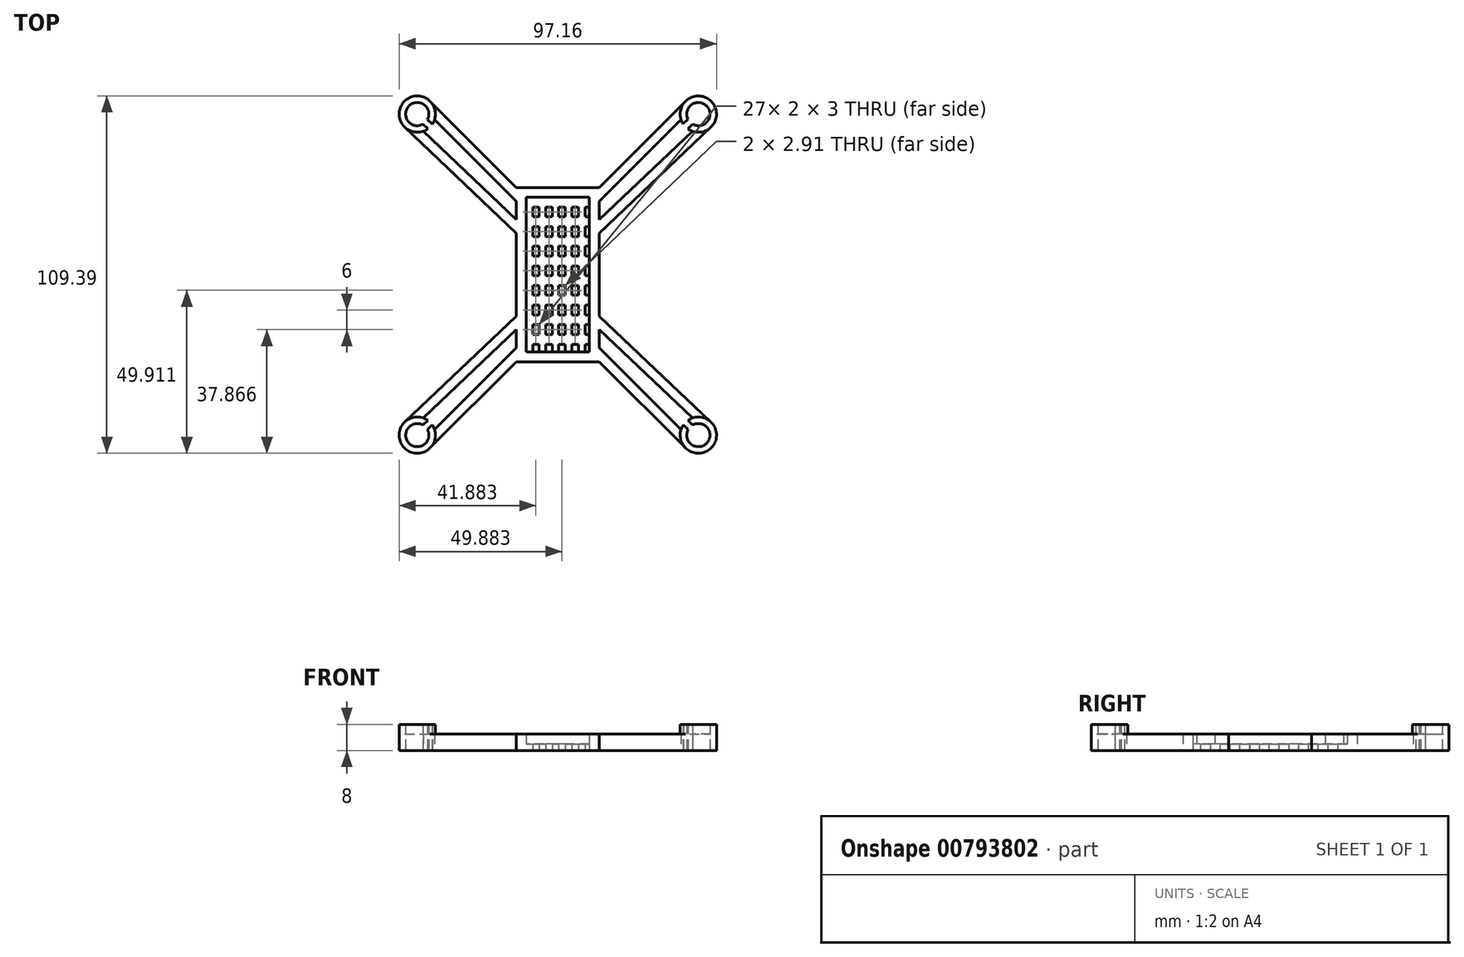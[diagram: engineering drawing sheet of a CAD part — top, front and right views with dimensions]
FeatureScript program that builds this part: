
annotation { "Feature Type Name" : "Feature", "Feature Type Description" : "" }
export const myFeature = defineFeature(function(context is Context, id is Id, definition is map)
    precondition{}
    {
        {
            var Q0;
            Q0=qCreatedBy(makeId("Top.planeOp"),FACE);
            var sketch = newSketch(context, id + "F0", { "sketchPlane" : qUnion([Q0])});
            skArc(sketch, "E0", {"start": v(4.6, 95.16) * mm, "mid": v(5, 95.85) * mm, "end": v(5.3, 96.6) * mm});
            skLineSegment(sketch, "E1", {"start": v(30.32, 71.56) * mm, "end": v(30.32, 65.97) * mm});
            skLineSegment(sketch, "E2", {"start": v(30.32, 22.47) * mm, "end": v(55.72, 22.47) * mm});
            skLineSegment(sketch, "E3", {"start": v(55.72, 26.7) * mm, "end": v(55.72, 32.3) * mm});
            skLineSegment(sketch, "E4", {"start": v(55.72, 75.8) * mm, "end": v(30.32, 75.8) * mm});
            skLineSegment(sketch, "E5", {"start": v(3.93, 102.2) * mm, "end": v(30.32, 75.8) * mm});
            skLineSegment(sketch, "E6", {"start": v(-3.82, 94.24) * mm, "end": v(30.32, 61.84) * mm});
            skLineSegment(sketch, "E7", {"start": v(55.72, 75.8) * mm, "end": v(82.12, 102.2) * mm});
            skLineSegment(sketch, "E8", {"start": v(55.72, 61.84) * mm, "end": v(89.87, 94.24) * mm});
            skArc(sketch, "E9", {"start": v(89.87, 94.24) * mm, "mid": v(90.03, 102.15) * mm, "end": v(82.12, 102.2) * mm});
            skLineSegment(sketch, "E10", {"start": v(30.32, 22.47) * mm, "end": v(3.93, -3.93) * mm});
            skLineSegment(sketch, "E11", {"start": v(30.32, 36.44) * mm, "end": v(-3.82, 4.03) * mm});
            skArc(sketch, "E12", {"start": v(5.3, 1.68) * mm, "mid": v(4.99, 2.45) * mm, "end": v(4.57, 3.17) * mm});
            skLineSegment(sketch, "E13", {"start": v(55.72, 22.47) * mm, "end": v(82.12, -3.93) * mm});
            skLineSegment(sketch, "E14", {"start": v(55.72, 36.44) * mm, "end": v(89.87, 4.03) * mm});
            skArc(sketch, "E15", {"start": v(84.23, 5.25) * mm, "mid": v(83.5, 4.94) * mm, "end": v(82.82, 4.52) * mm});
            skArc(sketch, "E16.0", {"start": v(3.15, 96.62) * mm, "mid": v(-2.55, 100.75) * mm, "end": v(1.74, 95.17) * mm});
            skArc(sketch, "E17.0", {"start": v(1.74, 3.1) * mm, "mid": v(-2.53, -2.5) * mm, "end": v(3.13, 1.7) * mm});
            skArc(sketch, "E18.0", {"start": v(84.31, 95.17) * mm, "mid": v(88.63, 100.72) * mm, "end": v(82.86, 96.7) * mm});
            skArc(sketch, "E19.0", {"start": v(82.9, 1.66) * mm, "mid": v(88.6, -2.48) * mm, "end": v(84.3, 3.1) * mm});
            skLineSegment(sketch, "E20.0", {"start": v(5.3, 96.6) * mm, "end": v(30.32, 71.56) * mm});
            skLineSegment(sketch, "E21.0", {"start": v(1.82, 93.02) * mm, "end": v(30.32, 65.97) * mm});
            skLineSegment(sketch, "E22.0", {"start": v(55.72, 71.56) * mm, "end": v(80.75, 96.6) * mm});
            skLineSegment(sketch, "E23.0", {"start": v(55.72, 65.97) * mm, "end": v(84.23, 93.02) * mm});
            skLineSegment(sketch, "E24.0", {"start": v(55.72, 32.3) * mm, "end": v(84.23, 5.25) * mm});
            skLineSegment(sketch, "E25.0", {"start": v(30.32, 32.3) * mm, "end": v(1.82, 5.25) * mm});
            skLineSegment(sketch, "E26.0", {"start": v(30.32, 26.7) * mm, "end": v(5.3, 1.68) * mm});
            skLineSegment(sketch, "E27.0", {"start": v(55.72, 26.7) * mm, "end": v(80.75, 1.68) * mm});
            skLineSegment(sketch, "E28", {"start": v(81.36, 95.28) * mm, "end": v(82.86, 96.7) * mm});
            skLineSegment(sketch, "E29", {"start": v(82.82, 93.75) * mm, "end": v(84.31, 95.17) * mm});
            skLineSegment(sketch, "E30", {"start": v(3.23, 93.75) * mm, "end": v(1.74, 95.17) * mm});
            skLineSegment(sketch, "E31", {"start": v(4.6, 95.16) * mm, "end": v(3.15, 96.62) * mm});
            skLineSegment(sketch, "E32", {"start": v(3.23, 4.52) * mm, "end": v(1.74, 3.1) * mm});
            skLineSegment(sketch, "E33", {"start": v(4.57, 3.17) * mm, "end": v(3.13, 1.7) * mm});
            skLineSegment(sketch, "E34", {"start": v(82.82, 4.52) * mm, "end": v(84.3, 3.1) * mm});
            skLineSegment(sketch, "E35", {"start": v(81.44, 3.11) * mm, "end": v(82.9, 1.66) * mm});
            skArc(sketch, "E36.trimOffspring", {"start": v(82.12, -3.93) * mm, "mid": v(90.03, -3.88) * mm, "end": v(89.87, 4.03) * mm});
            skArc(sketch, "E37.trimOffspring", {"start": v(81.44, 3.11) * mm, "mid": v(81.05, 2.42) * mm, "end": v(80.75, 1.68) * mm});
            skLineSegment(sketch, "E38.trimOffspring", {"start": v(55.72, 36.44) * mm, "end": v(55.72, 61.84) * mm});
            skLineSegment(sketch, "E39.trimOffspring", {"start": v(30.32, 61.84) * mm, "end": v(30.32, 36.44) * mm});
            skLineSegment(sketch, "E40.trimOffspring", {"start": v(55.72, 65.97) * mm, "end": v(55.72, 71.56) * mm});
            skLineSegment(sketch, "E41.trimOffspring", {"start": v(30.32, 32.3) * mm, "end": v(30.32, 26.7) * mm});
            skArc(sketch, "E42.trimOffspring", {"start": v(-3.82, 4.03) * mm, "mid": v(-3.98, -3.88) * mm, "end": v(3.93, -3.93) * mm});
            skArc(sketch, "E43.trimOffspring", {"start": v(3.23, 4.52) * mm, "mid": v(2.55, 4.94) * mm, "end": v(1.82, 5.25) * mm});
            skArc(sketch, "E44.trimOffspring", {"start": v(1.82, 93.02) * mm, "mid": v(2.55, 93.33) * mm, "end": v(3.23, 93.75) * mm});
            skArc(sketch, "E45.trimOffspring", {"start": v(3.93, 102.2) * mm, "mid": v(-3.98, 102.15) * mm, "end": v(-3.82, 94.24) * mm});
            skArc(sketch, "E46.trimOffspring", {"start": v(80.75, 96.6) * mm, "mid": v(81.01, 95.92) * mm, "end": v(81.36, 95.28) * mm});
            skArc(sketch, "E47.trimOffspring", {"start": v(82.82, 93.75) * mm, "mid": v(83.5, 93.33) * mm, "end": v(84.23, 93.02) * mm});
            skLineSegment(sketch, "E48", {"start": v(33.32, 72.8) * mm, "end": v(33.32, 25.47) * mm});
            skLineSegment(sketch, "E49", {"start": v(33.32, 25.47) * mm, "end": v(52.72, 25.47) * mm});
            skLineSegment(sketch, "E50", {"start": v(52.72, 25.47) * mm, "end": v(52.72, 72.8) * mm});
            skLineSegment(sketch, "E51", {"start": v(52.72, 72.8) * mm, "end": v(33.32, 72.8) * mm});
            skArc(sketch, "E52", {"start": v(84.23, 93.02) * mm, "mid": v(87.22, 92.84) * mm, "end": v(89.87, 94.24) * mm});
            skArc(sketch, "E53", {"start": v(82.12, 102.2) * mm, "mid": v(80.65, 99.59) * mm, "end": v(80.75, 96.6) * mm});
            skArc(sketch, "E54", {"start": v(5.3, 96.6) * mm, "mid": v(5.4, 99.59) * mm, "end": v(3.93, 102.2) * mm});
            skArc(sketch, "E55", {"start": v(-3.82, 94.24) * mm, "mid": v(-1.17, 92.84) * mm, "end": v(1.82, 93.02) * mm});
            skArc(sketch, "E56", {"start": v(3.93, -3.93) * mm, "mid": v(5.4, -1.32) * mm, "end": v(5.3, 1.68) * mm});
            skArc(sketch, "E57", {"start": v(1.82, 5.25) * mm, "mid": v(-1.17, 5.43) * mm, "end": v(-3.82, 4.03) * mm});
            skArc(sketch, "E58", {"start": v(80.75, 1.68) * mm, "mid": v(80.65, -1.32) * mm, "end": v(82.12, -3.93) * mm});
            skArc(sketch, "E59", {"start": v(89.87, 4.03) * mm, "mid": v(87.22, 5.43) * mm, "end": v(84.23, 5.25) * mm});
            skLineSegment(sketch, "E60.bottom", {"start": v(35.32, 69.8) * mm, "end": v(37.32, 69.8) * mm});
            skLineSegment(sketch, "E60.top", {"start": v(35.32, 66.8) * mm, "end": v(37.32, 66.8) * mm});
            skLineSegment(sketch, "E60.left", {"start": v(35.32, 69.8) * mm, "end": v(35.32, 66.8) * mm});
            skLineSegment(sketch, "E60.right", {"start": v(37.32, 69.8) * mm, "end": v(37.32, 66.8) * mm});
            skLineSegment(sketch, "E61.bottom", {"start": v(35.32, 63.8) * mm, "end": v(37.32, 63.8) * mm});
            skLineSegment(sketch, "E61.top", {"start": v(35.32, 60.8) * mm, "end": v(37.32, 60.8) * mm});
            skLineSegment(sketch, "E61.left", {"start": v(35.32, 63.8) * mm, "end": v(35.32, 60.8) * mm});
            skLineSegment(sketch, "E61.right", {"start": v(37.32, 63.8) * mm, "end": v(37.32, 60.8) * mm});
            skLineSegment(sketch, "E62.bottom", {"start": v(35.32, 57.8) * mm, "end": v(37.32, 57.8) * mm});
            skLineSegment(sketch, "E62.top", {"start": v(35.32, 54.8) * mm, "end": v(37.32, 54.8) * mm});
            skLineSegment(sketch, "E62.left", {"start": v(35.32, 57.8) * mm, "end": v(35.32, 54.8) * mm});
            skLineSegment(sketch, "E62.right", {"start": v(37.32, 57.8) * mm, "end": v(37.32, 54.8) * mm});
            skLineSegment(sketch, "E63.bottom", {"start": v(35.32, 51.8) * mm, "end": v(37.32, 51.8) * mm});
            skLineSegment(sketch, "E63.top", {"start": v(35.32, 48.8) * mm, "end": v(37.32, 48.8) * mm});
            skLineSegment(sketch, "E63.left", {"start": v(35.32, 51.8) * mm, "end": v(35.32, 48.8) * mm});
            skLineSegment(sketch, "E63.right", {"start": v(37.32, 51.8) * mm, "end": v(37.32, 48.8) * mm});
            skLineSegment(sketch, "E64.bottom", {"start": v(35.32, 45.8) * mm, "end": v(37.32, 45.8) * mm});
            skLineSegment(sketch, "E64.top", {"start": v(35.32, 42.8) * mm, "end": v(37.32, 42.8) * mm});
            skLineSegment(sketch, "E64.left", {"start": v(35.32, 45.8) * mm, "end": v(35.32, 42.8) * mm});
            skLineSegment(sketch, "E64.right", {"start": v(37.32, 45.8) * mm, "end": v(37.32, 42.8) * mm});
            skLineSegment(sketch, "E65.bottom", {"start": v(35.32, 39.8) * mm, "end": v(37.32, 39.8) * mm});
            skLineSegment(sketch, "E65.top", {"start": v(35.32, 36.8) * mm, "end": v(37.32, 36.8) * mm});
            skLineSegment(sketch, "E65.left", {"start": v(35.32, 39.8) * mm, "end": v(35.32, 36.8) * mm});
            skLineSegment(sketch, "E65.right", {"start": v(37.32, 39.8) * mm, "end": v(37.32, 36.8) * mm});
            skLineSegment(sketch, "E66.bottom", {"start": v(35.32, 33.8) * mm, "end": v(37.32, 33.8) * mm});
            skLineSegment(sketch, "E66.top", {"start": v(35.32, 30.8) * mm, "end": v(37.32, 30.8) * mm});
            skLineSegment(sketch, "E66.left", {"start": v(35.32, 33.8) * mm, "end": v(35.32, 30.8) * mm});
            skLineSegment(sketch, "E66.right", {"start": v(37.32, 33.8) * mm, "end": v(37.32, 30.8) * mm});
            skLineSegment(sketch, "E67.bottom", {"start": v(35.32, 27.8) * mm, "end": v(37.32, 27.8) * mm});
            skLineSegment(sketch, "E67.top", {"start": v(35.32, 25.47) * mm, "end": v(37.32, 25.47) * mm});
            skLineSegment(sketch, "E67.left", {"start": v(35.32, 27.8) * mm, "end": v(35.32, 25.47) * mm});
            skLineSegment(sketch, "E67.right", {"start": v(37.32, 27.8) * mm, "end": v(37.32, 25.47) * mm});
            skLineSegment(sketch, "E68.bottom", {"start": v(39.32, 27.8) * mm, "end": v(41.32, 27.8) * mm});
            skLineSegment(sketch, "E68.top", {"start": v(39.32, 25.47) * mm, "end": v(41.32, 25.47) * mm});
            skLineSegment(sketch, "E68.left", {"start": v(39.32, 27.8) * mm, "end": v(39.32, 25.47) * mm});
            skLineSegment(sketch, "E68.right", {"start": v(41.32, 27.8) * mm, "end": v(41.32, 25.47) * mm});
            skLineSegment(sketch, "E69.bottom", {"start": v(43.32, 27.8) * mm, "end": v(45.32, 27.8) * mm});
            skLineSegment(sketch, "E69.top", {"start": v(43.32, 25.47) * mm, "end": v(45.32, 25.47) * mm});
            skLineSegment(sketch, "E69.left", {"start": v(43.32, 27.8) * mm, "end": v(43.32, 25.47) * mm});
            skLineSegment(sketch, "E69.right", {"start": v(45.32, 27.8) * mm, "end": v(45.32, 25.47) * mm});
            skLineSegment(sketch, "E70.bottom", {"start": v(47.32, 27.8) * mm, "end": v(49.32, 27.8) * mm});
            skLineSegment(sketch, "E70.top", {"start": v(47.32, 25.47) * mm, "end": v(49.32, 25.47) * mm});
            skLineSegment(sketch, "E70.left", {"start": v(47.32, 27.8) * mm, "end": v(47.32, 25.47) * mm});
            skLineSegment(sketch, "E70.right", {"start": v(49.32, 27.8) * mm, "end": v(49.32, 25.47) * mm});
            skLineSegment(sketch, "E71.bottom", {"start": v(51.32, 27.8) * mm, "end": v(52.72, 27.8) * mm});
            skLineSegment(sketch, "E71.top", {"start": v(51.32, 25.47) * mm, "end": v(52.72, 25.47) * mm});
            skLineSegment(sketch, "E71.left", {"start": v(51.32, 27.8) * mm, "end": v(51.32, 25.47) * mm});
            skLineSegment(sketch, "E71.right", {"start": v(52.72, 27.8) * mm, "end": v(52.72, 25.47) * mm});
            skLineSegment(sketch, "E72.bottom", {"start": v(51.32, 33.8) * mm, "end": v(52.72, 33.8) * mm});
            skLineSegment(sketch, "E72.top", {"start": v(51.32, 30.8) * mm, "end": v(52.72, 30.8) * mm});
            skLineSegment(sketch, "E72.left", {"start": v(51.32, 33.8) * mm, "end": v(51.32, 30.8) * mm});
            skLineSegment(sketch, "E72.right", {"start": v(52.72, 33.8) * mm, "end": v(52.72, 30.8) * mm});
            skLineSegment(sketch, "E73.bottom", {"start": v(47.32, 33.8) * mm, "end": v(49.32, 33.8) * mm});
            skLineSegment(sketch, "E73.top", {"start": v(47.32, 30.8) * mm, "end": v(49.32, 30.8) * mm});
            skLineSegment(sketch, "E73.left", {"start": v(47.32, 33.8) * mm, "end": v(47.32, 30.8) * mm});
            skLineSegment(sketch, "E73.right", {"start": v(49.32, 33.8) * mm, "end": v(49.32, 30.8) * mm});
            skLineSegment(sketch, "E74.bottom", {"start": v(45.32, 33.8) * mm, "end": v(43.32, 33.8) * mm});
            skLineSegment(sketch, "E74.top", {"start": v(45.32, 30.8) * mm, "end": v(43.32, 30.8) * mm});
            skLineSegment(sketch, "E74.left", {"start": v(45.32, 33.8) * mm, "end": v(45.32, 30.8) * mm});
            skLineSegment(sketch, "E74.right", {"start": v(43.32, 33.8) * mm, "end": v(43.32, 30.8) * mm});
            skLineSegment(sketch, "E75.bottom", {"start": v(41.32, 33.8) * mm, "end": v(39.32, 33.8) * mm});
            skLineSegment(sketch, "E75.top", {"start": v(41.32, 30.8) * mm, "end": v(39.32, 30.8) * mm});
            skLineSegment(sketch, "E75.left", {"start": v(41.32, 33.8) * mm, "end": v(41.32, 30.8) * mm});
            skLineSegment(sketch, "E75.right", {"start": v(39.32, 33.8) * mm, "end": v(39.32, 30.8) * mm});
            skLineSegment(sketch, "E76.bottom", {"start": v(39.32, 36.8) * mm, "end": v(41.32, 36.8) * mm});
            skLineSegment(sketch, "E76.top", {"start": v(39.32, 39.8) * mm, "end": v(41.32, 39.8) * mm});
            skLineSegment(sketch, "E76.left", {"start": v(39.32, 36.8) * mm, "end": v(39.32, 39.8) * mm});
            skLineSegment(sketch, "E76.right", {"start": v(41.32, 36.8) * mm, "end": v(41.32, 39.8) * mm});
            skLineSegment(sketch, "E77.bottom", {"start": v(43.32, 39.8) * mm, "end": v(45.32, 39.8) * mm});
            skLineSegment(sketch, "E77.top", {"start": v(43.32, 36.8) * mm, "end": v(45.32, 36.8) * mm});
            skLineSegment(sketch, "E77.left", {"start": v(43.32, 39.8) * mm, "end": v(43.32, 36.8) * mm});
            skLineSegment(sketch, "E77.right", {"start": v(45.32, 39.8) * mm, "end": v(45.32, 36.8) * mm});
            skLineSegment(sketch, "E78.bottom", {"start": v(47.32, 36.8) * mm, "end": v(49.32, 36.8) * mm});
            skLineSegment(sketch, "E78.top", {"start": v(47.32, 39.8) * mm, "end": v(49.32, 39.8) * mm});
            skLineSegment(sketch, "E78.left", {"start": v(47.32, 36.8) * mm, "end": v(47.32, 39.8) * mm});
            skLineSegment(sketch, "E78.right", {"start": v(49.32, 36.8) * mm, "end": v(49.32, 39.8) * mm});
            skLineSegment(sketch, "E79.bottom", {"start": v(51.32, 39.8) * mm, "end": v(52.72, 39.8) * mm});
            skLineSegment(sketch, "E79.top", {"start": v(51.32, 36.8) * mm, "end": v(52.72, 36.8) * mm});
            skLineSegment(sketch, "E79.left", {"start": v(51.32, 39.8) * mm, "end": v(51.32, 36.8) * mm});
            skLineSegment(sketch, "E79.right", {"start": v(52.72, 39.8) * mm, "end": v(52.72, 36.8) * mm});
            skLineSegment(sketch, "E80.bottom", {"start": v(52.72, 42.8) * mm, "end": v(51.32, 42.8) * mm});
            skLineSegment(sketch, "E80.top", {"start": v(52.72, 45.8) * mm, "end": v(51.32, 45.8) * mm});
            skLineSegment(sketch, "E80.left", {"start": v(52.72, 42.8) * mm, "end": v(52.72, 45.8) * mm});
            skLineSegment(sketch, "E80.right", {"start": v(51.32, 42.8) * mm, "end": v(51.32, 45.8) * mm});
            skLineSegment(sketch, "E81.bottom", {"start": v(49.32, 45.8) * mm, "end": v(47.32, 45.8) * mm});
            skLineSegment(sketch, "E81.top", {"start": v(49.32, 42.8) * mm, "end": v(47.32, 42.8) * mm});
            skLineSegment(sketch, "E81.left", {"start": v(49.32, 45.8) * mm, "end": v(49.32, 42.8) * mm});
            skLineSegment(sketch, "E81.right", {"start": v(47.32, 45.8) * mm, "end": v(47.32, 42.8) * mm});
            skLineSegment(sketch, "E82.bottom", {"start": v(45.32, 42.9) * mm, "end": v(43.32, 42.9) * mm});
            skLineSegment(sketch, "E82.top", {"start": v(45.32, 45.8) * mm, "end": v(43.32, 45.8) * mm});
            skLineSegment(sketch, "E82.left", {"start": v(45.32, 42.9) * mm, "end": v(45.32, 45.8) * mm});
            skLineSegment(sketch, "E82.right", {"start": v(43.32, 42.9) * mm, "end": v(43.32, 45.8) * mm});
            skLineSegment(sketch, "E83.bottom", {"start": v(41.32, 45.8) * mm, "end": v(39.32, 45.8) * mm});
            skLineSegment(sketch, "E83.top", {"start": v(41.32, 42.8) * mm, "end": v(39.32, 42.8) * mm});
            skLineSegment(sketch, "E83.left", {"start": v(41.32, 45.8) * mm, "end": v(41.32, 42.8) * mm});
            skLineSegment(sketch, "E83.right", {"start": v(39.32, 45.8) * mm, "end": v(39.32, 42.8) * mm});
            skLineSegment(sketch, "E84.bottom", {"start": v(39.32, 51.8) * mm, "end": v(41.32, 51.8) * mm});
            skLineSegment(sketch, "E84.top", {"start": v(39.32, 48.8) * mm, "end": v(41.32, 48.8) * mm});
            skLineSegment(sketch, "E84.left", {"start": v(39.32, 51.8) * mm, "end": v(39.32, 48.8) * mm});
            skLineSegment(sketch, "E84.right", {"start": v(41.32, 51.8) * mm, "end": v(41.32, 48.8) * mm});
            skLineSegment(sketch, "E85.bottom", {"start": v(43.32, 48.8) * mm, "end": v(45.32, 48.8) * mm});
            skLineSegment(sketch, "E85.top", {"start": v(43.32, 51.8) * mm, "end": v(45.32, 51.8) * mm});
            skLineSegment(sketch, "E85.left", {"start": v(43.32, 48.8) * mm, "end": v(43.32, 51.8) * mm});
            skLineSegment(sketch, "E85.right", {"start": v(45.32, 48.8) * mm, "end": v(45.32, 51.8) * mm});
            skLineSegment(sketch, "E86.bottom", {"start": v(47.32, 51.8) * mm, "end": v(49.32, 51.8) * mm});
            skLineSegment(sketch, "E86.top", {"start": v(47.32, 48.8) * mm, "end": v(49.32, 48.8) * mm});
            skLineSegment(sketch, "E86.left", {"start": v(47.32, 51.8) * mm, "end": v(47.32, 48.8) * mm});
            skLineSegment(sketch, "E86.right", {"start": v(49.32, 51.8) * mm, "end": v(49.32, 48.8) * mm});
            skLineSegment(sketch, "E87.bottom", {"start": v(51.4, 51.8) * mm, "end": v(52.72, 51.8) * mm});
            skLineSegment(sketch, "E87.top", {"start": v(51.4, 48.8) * mm, "end": v(52.72, 48.8) * mm});
            skLineSegment(sketch, "E87.left", {"start": v(51.4, 51.8) * mm, "end": v(51.4, 48.8) * mm});
            skLineSegment(sketch, "E87.right", {"start": v(52.72, 51.8) * mm, "end": v(52.72, 48.8) * mm});
            skLineSegment(sketch, "E88.bottom", {"start": v(52.72, 54.8) * mm, "end": v(51.32, 54.8) * mm});
            skLineSegment(sketch, "E88.top", {"start": v(52.72, 57.8) * mm, "end": v(51.32, 57.8) * mm});
            skLineSegment(sketch, "E88.left", {"start": v(52.72, 54.8) * mm, "end": v(52.72, 57.8) * mm});
            skLineSegment(sketch, "E88.right", {"start": v(51.32, 54.8) * mm, "end": v(51.32, 57.8) * mm});
            skLineSegment(sketch, "E89.bottom", {"start": v(49.32, 57.8) * mm, "end": v(47.32, 57.8) * mm});
            skLineSegment(sketch, "E89.top", {"start": v(49.32, 54.8) * mm, "end": v(47.32, 54.8) * mm});
            skLineSegment(sketch, "E89.left", {"start": v(49.32, 57.8) * mm, "end": v(49.32, 54.8) * mm});
            skLineSegment(sketch, "E89.right", {"start": v(47.32, 57.8) * mm, "end": v(47.32, 54.8) * mm});
            skLineSegment(sketch, "E90.bottom", {"start": v(45.32, 54.8) * mm, "end": v(43.32, 54.8) * mm});
            skLineSegment(sketch, "E90.top", {"start": v(45.32, 57.8) * mm, "end": v(43.32, 57.8) * mm});
            skLineSegment(sketch, "E90.left", {"start": v(45.32, 54.8) * mm, "end": v(45.32, 57.8) * mm});
            skLineSegment(sketch, "E90.right", {"start": v(43.32, 54.8) * mm, "end": v(43.32, 57.8) * mm});
            skLineSegment(sketch, "E91.bottom", {"start": v(41.32, 57.8) * mm, "end": v(39.32, 57.8) * mm});
            skLineSegment(sketch, "E91.top", {"start": v(41.32, 54.8) * mm, "end": v(39.32, 54.8) * mm});
            skLineSegment(sketch, "E91.left", {"start": v(41.32, 57.8) * mm, "end": v(41.32, 54.8) * mm});
            skLineSegment(sketch, "E91.right", {"start": v(39.32, 57.8) * mm, "end": v(39.32, 54.8) * mm});
            skLineSegment(sketch, "E92.bottom", {"start": v(39.32, 60.8) * mm, "end": v(41.32, 60.8) * mm});
            skLineSegment(sketch, "E92.top", {"start": v(39.32, 63.8) * mm, "end": v(41.32, 63.8) * mm});
            skLineSegment(sketch, "E92.left", {"start": v(39.32, 60.8) * mm, "end": v(39.32, 63.8) * mm});
            skLineSegment(sketch, "E92.right", {"start": v(41.32, 60.8) * mm, "end": v(41.32, 63.8) * mm});
            skLineSegment(sketch, "E93.bottom", {"start": v(43.32, 63.8) * mm, "end": v(45.32, 63.8) * mm});
            skLineSegment(sketch, "E93.top", {"start": v(43.32, 60.8) * mm, "end": v(45.32, 60.8) * mm});
            skLineSegment(sketch, "E93.left", {"start": v(43.32, 63.8) * mm, "end": v(43.32, 60.8) * mm});
            skLineSegment(sketch, "E93.right", {"start": v(45.32, 63.8) * mm, "end": v(45.32, 60.8) * mm});
            skLineSegment(sketch, "E94.bottom", {"start": v(47.32, 63.8) * mm, "end": v(49.32, 63.8) * mm});
            skLineSegment(sketch, "E94.top", {"start": v(47.32, 60.8) * mm, "end": v(49.32, 60.8) * mm});
            skLineSegment(sketch, "E94.left", {"start": v(47.32, 63.8) * mm, "end": v(47.32, 60.8) * mm});
            skLineSegment(sketch, "E94.right", {"start": v(49.32, 63.8) * mm, "end": v(49.32, 60.8) * mm});
            skLineSegment(sketch, "E95.bottom", {"start": v(51.32, 60.8) * mm, "end": v(52.72, 60.8) * mm});
            skLineSegment(sketch, "E95.top", {"start": v(51.32, 63.8) * mm, "end": v(52.72, 63.8) * mm});
            skLineSegment(sketch, "E95.left", {"start": v(51.32, 60.8) * mm, "end": v(51.32, 63.8) * mm});
            skLineSegment(sketch, "E95.right", {"start": v(52.72, 60.8) * mm, "end": v(52.72, 63.8) * mm});
            skLineSegment(sketch, "E96.bottom", {"start": v(51.32, 66.8) * mm, "end": v(52.72, 66.8) * mm});
            skLineSegment(sketch, "E96.top", {"start": v(51.32, 69.8) * mm, "end": v(52.72, 69.8) * mm});
            skLineSegment(sketch, "E96.left", {"start": v(51.32, 66.8) * mm, "end": v(51.32, 69.8) * mm});
            skLineSegment(sketch, "E96.right", {"start": v(52.72, 66.8) * mm, "end": v(52.72, 69.8) * mm});
            skLineSegment(sketch, "E97.bottom", {"start": v(49.32, 69.8) * mm, "end": v(47.32, 69.8) * mm});
            skLineSegment(sketch, "E97.top", {"start": v(49.32, 66.8) * mm, "end": v(47.32, 66.8) * mm});
            skLineSegment(sketch, "E97.left", {"start": v(49.32, 69.8) * mm, "end": v(49.32, 66.8) * mm});
            skLineSegment(sketch, "E97.right", {"start": v(47.32, 69.8) * mm, "end": v(47.32, 66.8) * mm});
            skLineSegment(sketch, "E98.bottom", {"start": v(45.32, 66.8) * mm, "end": v(43.32, 66.8) * mm});
            skLineSegment(sketch, "E98.top", {"start": v(45.32, 69.8) * mm, "end": v(43.32, 69.8) * mm});
            skLineSegment(sketch, "E98.left", {"start": v(45.32, 66.8) * mm, "end": v(45.32, 69.8) * mm});
            skLineSegment(sketch, "E98.right", {"start": v(43.32, 66.8) * mm, "end": v(43.32, 69.8) * mm});
            skLineSegment(sketch, "E99.bottom", {"start": v(41.32, 69.8) * mm, "end": v(39.32, 69.8) * mm});
            skLineSegment(sketch, "E99.top", {"start": v(41.32, 66.8) * mm, "end": v(39.32, 66.8) * mm});
            skLineSegment(sketch, "E99.left", {"start": v(41.32, 69.8) * mm, "end": v(41.32, 66.8) * mm});
            skLineSegment(sketch, "E99.right", {"start": v(39.32, 69.8) * mm, "end": v(39.32, 66.8) * mm});
            skSolve(sketch);
        }
        {
            var Q0;
            Q0=makeQuery(id+"F0.imprint","IMPRINT",FACE,{"disambiguationData":[TD([[makeQuery(id+"F0.imprint","IMPRINT",EDGE,{"derivedFrom":sQuery(id+"F0.wireOp",EDGE,"E1")}),1.0]])]});
            extrude(context, id + "F1", {"entities" : qUnion([Q0]), "depth" : 5 * mm, "offsetDistance" : 25.4 * mm});
        }
        {
            var Q0;
            Q0=makeQuery(id+"F0.imprint","IMPRINT",FACE,{"disambiguationData":[TD([[makeQuery(id+"F0.imprint","IMPRINT",EDGE,{"derivedFrom":sQuery(id+"F0.wireOp",EDGE,"E48")}),1.0]])]});
            extrude(context, id + "F2", {"entities" : qUnion([Q0]), "operationType" : NewBodyOperationType.ADD, "depth" : 2 * mm, "offsetDistance" : 25.4 * mm});
        }
        {
            var Q0;
            Q0=makeQuery(id+"F0.imprint","IMPRINT",FACE,{"disambiguationData":[TD([[makeQuery(id+"F0.imprint","IMPRINT",EDGE,{"derivedFrom":sQuery(id+"F0.wireOp",EDGE,"E0")}),1.0]])]});
            var Q1;
            Q1=makeQuery(id+"F0.imprint","IMPRINT",FACE,{"disambiguationData":[TD([[makeQuery(id+"F0.imprint","IMPRINT",EDGE,{"derivedFrom":sQuery(id+"F0.wireOp",EDGE,"E9")}),1.0]])]});
            var Q2;
            Q2=makeQuery(id+"F0.imprint","IMPRINT",FACE,{"disambiguationData":[TD([[makeQuery(id+"F0.imprint","IMPRINT",EDGE,{"derivedFrom":sQuery(id+"F0.wireOp",EDGE,"E15")}),1.0]])]});
            var Q3;
            Q3=makeQuery(id+"F0.imprint","IMPRINT",FACE,{"disambiguationData":[TD([[makeQuery(id+"F0.imprint","IMPRINT",EDGE,{"derivedFrom":sQuery(id+"F0.wireOp",EDGE,"E12")}),1.0]])]});
            extrude(context, id + "F3", {"entities" : qUnion([Q0, Q1, Q2, Q3]), "operationType" : NewBodyOperationType.ADD, "depth" : 8 * mm, "offsetDistance" : 25.4 * mm});
        }
    });
